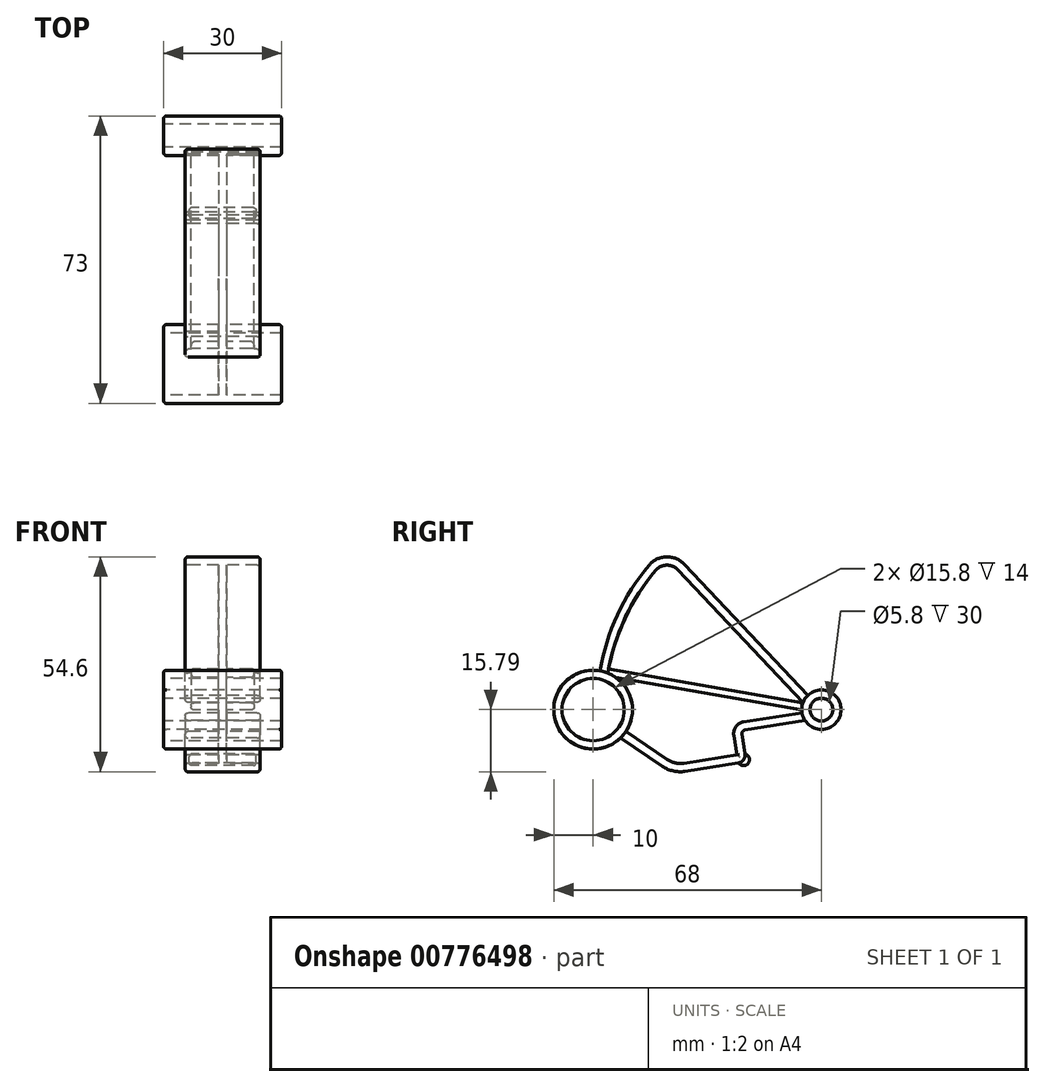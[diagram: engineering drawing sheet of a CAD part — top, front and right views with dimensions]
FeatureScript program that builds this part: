
annotation { "Feature Type Name" : "Feature", "Feature Type Description" : "" }
export const myFeature = defineFeature(function(context is Context, id is Id, definition is map)
    precondition{}
    {
        {
            var Q0;
            Q0=qCreatedBy(makeId("Right.planeOp"),FACE);
            var sketch = newSketch(context, id + "F0", { "sketchPlane" : qUnion([Q0])});
            skCircle(sketch, "E0", {"center": v(-58, 0) * mm, "radius": 10 * mm});
            skCircle(sketch, "E1", {"center": v(0, 0) * mm, "radius": 5 * mm});
            skLineSegment(sketch, "E2", {"start": v(-56.28, 9.85) * mm, "end": v(-4.93, 0.86) * mm, "construction": true});
            skLineSegment(sketch, "E3", {"start": v(-4.94, -0.78) * mm, "end": v(-19.76, -3.12) * mm});
            skLineSegment(sketch, "E4", {"start": v(-21.47, -11.49) * mm, "end": v(-34.94, -13.61) * mm});
            skLineSegment(sketch, "E5", {"start": v(-39.23, -12.66) * mm, "end": v(-49.71, -5.6) * mm});
            skLineSegment(sketch, "E6", {"start": v(-21.47, -11.49) * mm, "end": v(-22.25, -6.55) * mm});
            skLineSegment(sketch, "E7", {"start": v(-3.43, 3.64) * mm, "end": v(-34.85, 36.93) * mm});
            skArc(sketch, "E8", {"start": v(-56.28, 9.85) * mm, "mid": v(-51.81, 24.08) * mm, "end": v(-43.82, 36.66) * mm});
            skPoint(sketch, "E9.visualSharp", {"position": v(-39.21, 41.55) * mm});
            skArc(sketch, "E9.filletArc", {"start": v(-34.85, 36.93) * mm, "mid": v(-39.4, 38.8) * mm, "end": v(-43.82, 36.66) * mm});
            skPoint(sketch, "E10.visualSharp", {"position": v(-37.28, -13.98) * mm});
            skArc(sketch, "E10.filletArc", {"start": v(-39.23, -12.66) * mm, "mid": v(-37.18, -13.54) * mm, "end": v(-34.94, -13.61) * mm});
            skPoint(sketch, "E11.visualSharp", {"position": v(-22.72, -3.59) * mm});
            skArc(sketch, "E11.filletArc", {"start": v(-19.76, -3.12) * mm, "mid": v(-21.71, -4.32) * mm, "end": v(-22.25, -6.55) * mm});
            skCircle(sketch, "E12", {"center": v(0, 0) * mm, "radius": 2.9 * mm});
            skCircle(sketch, "E13", {"center": v(-58, 0) * mm, "radius": 7.9 * mm});
            skArc(sketch, "E14.1", {"start": v(-54.25, 9.27) * mm, "mid": v(-49.95, 23.09) * mm, "end": v(-42.2, 35.31) * mm});
            skArc(sketch, "E14.2", {"start": v(-36.38, 35.49) * mm, "mid": v(-39.33, 36.7) * mm, "end": v(-42.2, 35.31) * mm});
            skLineSegment(sketch, "E14.3", {"start": v(-4.64, 1.86) * mm, "end": v(-36.38, 35.49) * mm});
            skLineSegment(sketch, "E15.0", {"start": v(-40.4, -14.4) * mm, "end": v(-51.07, -7.2) * mm});
            skArc(sketch, "E15.1", {"start": v(-40.4, -14.4) * mm, "mid": v(-37.63, -15.6) * mm, "end": v(-34.62, -15.69) * mm});
            skLineSegment(sketch, "E15.2", {"start": v(-4.15, -2.78) * mm, "end": v(-19.43, -5.2) * mm});
            skArc(sketch, "E15.3", {"start": v(-19.43, -5.2) * mm, "mid": v(-20.02, -5.55) * mm, "end": v(-20.18, -6.22) * mm});
            skLineSegment(sketch, "E16", {"start": v(-54.04, 10.4) * mm, "end": v(-4.52, 1.73) * mm});
            skLineSegment(sketch, "E17", {"start": v(-52.3, 8.21) * mm, "end": v(-5, -0.06) * mm});
            skLineSegment(sketch, "E18", {"start": v(-19.4, -11.16) * mm, "end": v(-20.18, -6.22) * mm});
            skLineSegment(sketch, "E19", {"start": v(-21.14, -13.56) * mm, "end": v(-34.62, -15.69) * mm});
            skPoint(sketch, "E20.visualSharp", {"position": v(-19.07, -13.23) * mm});
            skArc(sketch, "E20.filletArc", {"start": v(-21.14, -13.56) * mm, "mid": v(-19.77, -12.72) * mm, "end": v(-19.4, -11.16) * mm});
            skCircle(sketch, "E21", {"center": v(-19.77, -12.72) * mm, "radius": 1.5 * mm});
            skSolve(sketch);
        }
        {
            var Q0;
            Q0=makeQuery(id+"F0.imprint","IMPRINT",FACE,{"disambiguationData":[TD([[makeQuery(id+"F0.imprint","IMPRINT",EDGE,{"derivedFrom":sQuery(id+"F0.wireOp",EDGE,"E13")}),-1.0]])]});
            var Q1;
            Q1=makeQuery(id+"F0.imprint","IMPRINT",FACE,{"disambiguationData":[TD([[makeQuery(id+"F0.imprint","IMPRINT",EDGE,{"derivedFrom":sQuery(id+"F0.wireOp",EDGE,"E12")}),-1.0]])]});
            extrude(context, id + "F1", {"entities" : qUnion([Q0, Q1]), "endBound" : BoundingType.SYMMETRIC, "depth" : 30 * mm, "offsetDistance" : 25 * mm});
        }
        {
            var Q0;
            {var subQ0=sQuery(id+"F0.wireOp",EDGE,"E14.2");Q0=makeQuery(id+"F0.imprint","IMPRINT",FACE,{"disambiguationData":[TD([[makeQuery(id+"F0.imprint","IMPRINT",EDGE,{"derivedFrom":subQ0}),1.0]])]});}
            var Q1;
            {var subQ5=sQuery(id+"F0.wireOp",EDGE,"E17");Q1=makeQuery(id+"F0.imprint","IMPRINT",FACE,{"disambiguationData":[TD([[makeQuery(id+"F0.imprint","IMPRINT",EDGE,{"derivedFrom":subQ5}),1.0]])]});}
            var Q2;
            {var subQ0=sQuery(id+"F0.wireOp",EDGE,"E3");Q2=makeQuery(id+"F0.imprint","IMPRINT",FACE,{"disambiguationData":[TD([[makeQuery(id+"F0.imprint","IMPRINT",EDGE,{"derivedFrom":subQ0}),-1.0]])]});}
            var Q3;
            Q3=makeQuery(id+"F0.imprint","IMPRINT",FACE,{"disambiguationData":[TD([[makeQuery(id+"F0.imprint","IMPRINT",EDGE,{"derivedFrom":sQuery(id+"F0.wireOp",EDGE,"E13")}),1.0]])]});
            extrude(context, id + "F2", {"entities" : qUnion([Q0, Q1, Q2, Q3]), "operationType" : NewBodyOperationType.ADD, "endBound" : BoundingType.SYMMETRIC, "depth" : 2 * mm, "offsetDistance" : 25 * mm});
        }
        {
            var Q0;
            {var subQ0=sQuery(id+"F0.wireOp",EDGE,"E7");Q0=makeQuery(id+"F0.imprint","IMPRINT",FACE,{"disambiguationData":[TD([[makeQuery(id+"F0.imprint","IMPRINT",EDGE,{"derivedFrom":subQ0}),1.0]])]});}
            var Q1;
            {var subQ8=sQuery(id+"F0.wireOp",EDGE,"E3");Q1=makeQuery(id+"F0.imprint","IMPRINT",FACE,{"disambiguationData":[TD([[makeQuery(id+"F0.imprint","IMPRINT",EDGE,{"derivedFrom":subQ8}),1.0]])]});}
            var Q2;
            {var subQ0=sQuery(id+"F0.wireOp",EDGE,"E21");var subQ1=sQuery(id+"F0.wireOp",EDGE,"E20.filletArc");var subQ2=makeQuery(id+"F0.imprint","INTERSECT",VERTEX,{"disambiguationData":[OD(0.0)],"derivedFrom":[subQ1,subQ0]});Q2=makeQuery(id+"F0.imprint","IMPRINT",FACE,{"disambiguationData":[TD([[makeQuery(id+"F0.imprint","IMPRINT",EDGE,{"disambiguationData":[TD([[subQ2,-1.0]])],"derivedFrom":subQ1}),1.0]])]});}
            extrude(context, id + "F3", {"entities" : qUnion([Q0, Q1, Q2]), "operationType" : NewBodyOperationType.ADD, "endBound" : BoundingType.SYMMETRIC, "depth" : 19 * mm, "offsetDistance" : 25 * mm});
        }
        {
            var Q0;
            {var subQ5=sQuery(id+"F0.wireOp",EDGE,"E17");Q0=makeQuery(id+"F0.imprint","IMPRINT",FACE,{"disambiguationData":[TD([[makeQuery(id+"F0.imprint","IMPRINT",EDGE,{"derivedFrom":subQ5}),1.0]])]});}
            extrude(context, id + "F4", {"entities" : qUnion([Q0]), "operationType" : NewBodyOperationType.ADD, "endBound" : BoundingType.SYMMETRIC, "depth" : 16 * mm, "offsetDistance" : 25 * mm});
        }
        {
            var Q0;
            {var subQ0=sQuery(id+"F0.wireOp",EDGE,"E21");var subQ1=sQuery(id+"F0.wireOp",EDGE,"E20.filletArc");var subQ2=makeQuery(id+"F0.imprint","INTERSECT",VERTEX,{"disambiguationData":[OD(0.0)],"derivedFrom":[subQ1,subQ0]});Q0=makeQuery(id+"F0.imprint","IMPRINT",FACE,{"disambiguationData":[TD([[makeQuery(id+"F0.imprint","IMPRINT",EDGE,{"disambiguationData":[TD([[subQ2,-1.0]])],"derivedFrom":subQ1}),-1.0]])]});}
            extrude(context, id + "F5", {"entities" : qUnion([Q0]), "operationType" : NewBodyOperationType.ADD, "endBound" : BoundingType.SYMMETRIC, "depth" : 17 * mm, "offsetDistance" : 25 * mm});
        }
        {
            var Q0;
            Q0=makeQuery(id+"F3.opExtrude","CAP_EDGE",EDGE,{"disambiguationData":[OSD([sQuery(id+"F0.wireOp",EDGE,"E14.1")])],"isStart":false});
            var Q1;
            Q1=makeQuery(id+"F3.opExtrude","CAP_EDGE",EDGE,{"disambiguationData":[OSD([sQuery(id+"F0.wireOp",EDGE,"E8")])],"isStart":false});
            var Q2;
            Q2=makeQuery(id+"F3.opExtrude","CAP_EDGE",EDGE,{"disambiguationData":[OSD([sQuery(id+"F0.wireOp",EDGE,"E15.0")])],"isStart":false});
            var Q3;
            Q3=makeQuery(id+"F3.opExtrude","CAP_EDGE",EDGE,{"disambiguationData":[OSD([sQuery(id+"F0.wireOp",EDGE,"E15.1")])],"isStart":false});
            var Q4;
            Q4=makeQuery(id+"F3.opExtrude","CAP_EDGE",EDGE,{"disambiguationData":[OSD([sQuery(id+"F0.wireOp",EDGE,"E21")])],"isStart":false});
            var Q5;
            Q5=makeQuery(id+"F3.opExtrude","CAP_EDGE",EDGE,{"disambiguationData":[OSD([sQuery(id+"F0.wireOp",EDGE,"E18")])],"isStart":false});
            var Q6;
            Q6=makeQuery(id+"F3.opExtrude","CAP_EDGE",EDGE,{"disambiguationData":[OSD([sQuery(id+"F0.wireOp",EDGE,"E11.filletArc")])],"isStart":false});
            var Q7;
            Q7=makeQuery(id+"F4.opExtrude","CAP_EDGE",EDGE,{"disambiguationData":[OSD([sQuery(id+"F0.wireOp",EDGE,"E17")])],"isStart":false});
            var Q8;
            Q8=makeQuery(id+"F4.opExtrude","CAP_EDGE",EDGE,{"disambiguationData":[OSD([sQuery(id+"F0.wireOp",EDGE,"E16")])],"isStart":false});
            var Q9;
            Q9=makeQuery(id+"F3.opExtrude","CAP_EDGE",EDGE,{"disambiguationData":[OSD([sQuery(id+"F0.wireOp",EDGE,"E5")])],"isStart":true});
            var Q10;
            Q10=makeQuery(id+"F3.opExtrude","CAP_EDGE",EDGE,{"disambiguationData":[OSD([sQuery(id+"F0.wireOp",EDGE,"E6")])],"isStart":true});
            var Q11;
            Q11=makeQuery(id+"F3.opExtrude","CAP_EDGE",EDGE,{"disambiguationData":[OSD([sQuery(id+"F0.wireOp",EDGE,"E15.0")])],"isStart":true});
            var Q12;
            Q12=makeQuery(id+"F3.opExtrude","CAP_EDGE",EDGE,{"disambiguationData":[OSD([sQuery(id+"F0.wireOp",EDGE,"E19")])],"isStart":true});
            var Q13;
            Q13=makeQuery(id+"F3.opExtrude","CAP_EDGE",EDGE,{"disambiguationData":[OSD([sQuery(id+"F0.wireOp",EDGE,"E15.1")])],"isStart":true});
            var Q14;
            Q14=makeQuery(id+"F3.opExtrude","CAP_EDGE",EDGE,{"disambiguationData":[OSD([sQuery(id+"F0.wireOp",EDGE,"E21")])],"isStart":true});
            var Q15;
            Q15=makeQuery(id+"F3.opExtrude","CAP_EDGE",EDGE,{"disambiguationData":[OSD([sQuery(id+"F0.wireOp",EDGE,"E18")])],"isStart":true});
            var Q16;
            Q16=makeQuery(id+"F3.opExtrude","CAP_EDGE",EDGE,{"disambiguationData":[OSD([sQuery(id+"F0.wireOp",EDGE,"E14.3")])],"isStart":true});
            var Q17;
            Q17=makeQuery(id+"F3.opExtrude","CAP_EDGE",EDGE,{"disambiguationData":[OSD([sQuery(id+"F0.wireOp",EDGE,"E7")])],"isStart":true});
            var Q18;
            Q18=makeQuery(id+"F4.opExtrude","CAP_EDGE",EDGE,{"disambiguationData":[OSD([sQuery(id+"F0.wireOp",EDGE,"E17")])],"isStart":true});
            var Q19;
            Q19=makeQuery(id+"F4.opExtrude","CAP_EDGE",EDGE,{"disambiguationData":[OSD([sQuery(id+"F0.wireOp",EDGE,"E16")])],"isStart":true});
            var Q20;
            Q20=makeQuery(id+"F1.opExtrude","CAP_EDGE",EDGE,{"disambiguationData":[OSD([sQuery(id+"F0.wireOp",EDGE,"E1")])],"isStart":true});
            var Q21;
            Q21=makeQuery(id+"F1.opExtrude","CAP_EDGE",EDGE,{"disambiguationData":[OSD([sQuery(id+"F0.wireOp",EDGE,"E1")])],"isStart":false});
            var Q22;
            Q22=makeQuery(id+"F1.opExtrude","CAP_EDGE",EDGE,{"disambiguationData":[OSD([sQuery(id+"F0.wireOp",EDGE,"E0")])],"isStart":true});
            var Q23;
            Q23=makeQuery(id+"F1.opExtrude","CAP_EDGE",EDGE,{"disambiguationData":[OSD([sQuery(id+"F0.wireOp",EDGE,"E0")])],"isStart":false});
            var Q24;
            Q24=makeQuery(id+"F5.opExtrude","CAP_EDGE",EDGE,{"disambiguationData":[OSD([sQuery(id+"F0.wireOp",EDGE,"E21")])],"isStart":false});
            var Q25;
            Q25=makeQuery(id+"F5.opExtrude","CAP_EDGE",EDGE,{"disambiguationData":[OSD([sQuery(id+"F0.wireOp",EDGE,"E21")])],"isStart":true});
            fillet(context, id + "F6", {"entities" : qUnion([Q0, Q1, Q2, Q3, Q4, Q5, Q6, Q7, Q8, Q9, Q10, Q11, Q12, Q13, Q14, Q15, Q16, Q17, Q18, Q19, Q20, Q21, Q22, Q23, Q24, Q25]), "radius" : .7 * mm, "tangentPropagation" : true, "allowEdgeOverflow" : false});
        }
    });
